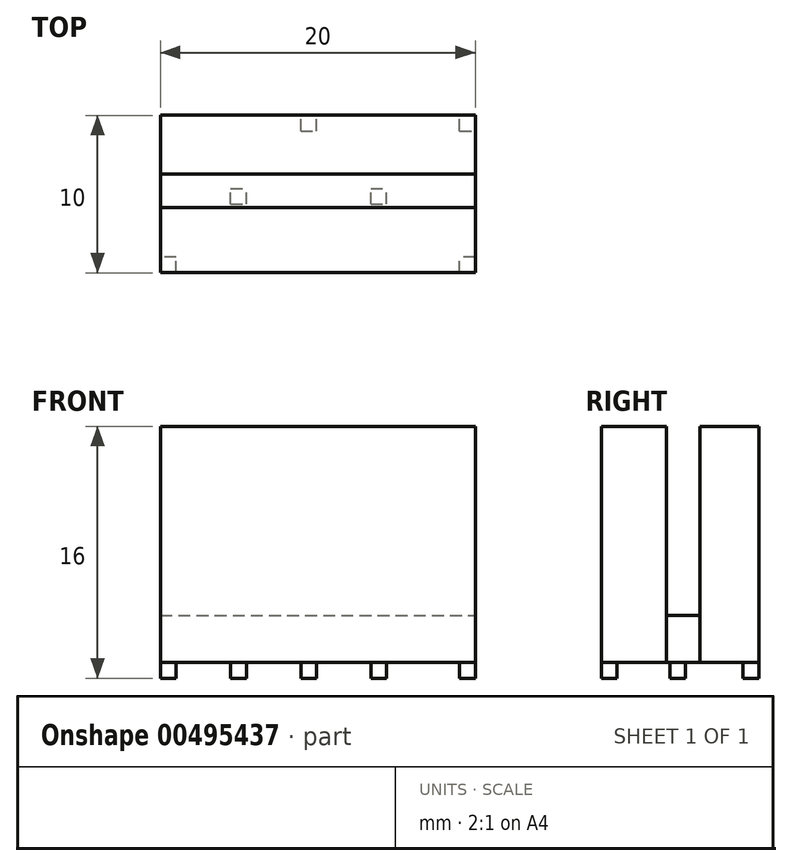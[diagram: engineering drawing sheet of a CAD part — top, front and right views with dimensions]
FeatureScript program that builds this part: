
annotation { "Feature Type Name" : "Feature", "Feature Type Description" : "" }
export const myFeature = defineFeature(function(context is Context, id is Id, definition is map)
    precondition{}
    {
        {
            var Q0;
            Q0=qCreatedBy(makeId("Top.planeOp"),FACE);
            var sketch = newSketch(context, id + "F0", { "sketchPlane" : qUnion([Q0])});
            skLineSegment(sketch, "E0.bottom", {"start": v(-25.14, 12.9) * mm, "end": v(-5.14, 12.9) * mm});
            skLineSegment(sketch, "E0.top", {"start": v(-25.14, 2.9) * mm, "end": v(-5.14, 2.9) * mm});
            skLineSegment(sketch, "E0.left", {"start": v(-25.14, 12.9) * mm, "end": v(-25.14, 2.9) * mm});
            skLineSegment(sketch, "E0.right", {"start": v(-5.14, 12.9) * mm, "end": v(-5.14, 2.9) * mm});
            skLineSegment(sketch, "E1.bottom", {"start": v(-25.14, 9.18) * mm, "end": v(-5.14, 9.18) * mm});
            skLineSegment(sketch, "E1.top", {"start": v(-25.14, 7.05) * mm, "end": v(-5.14, 7.05) * mm});
            skLineSegment(sketch, "E1.left", {"start": v(-25.14, 9.18) * mm, "end": v(-25.14, 7.05) * mm});
            skLineSegment(sketch, "E1.right", {"start": v(-5.14, 9.18) * mm, "end": v(-5.14, 7.05) * mm});
            skSolve(sketch);
        }
        {
            var Q0;
            {var subQ0=sQuery(id+"F0.wireOp",EDGE,"E0.bottom");Q0=makeQuery(id+"F0.imprint","IMPRINT",FACE,{"disambiguationData":[TD([[makeQuery(id+"F0.imprint","IMPRINT",EDGE,{"derivedFrom":subQ0}),-1.0]])]});}
            var Q1;
            {var subQ0=sQuery(id+"F0.wireOp",EDGE,"E0.top");Q1=makeQuery(id+"F0.imprint","IMPRINT",FACE,{"disambiguationData":[TD([[makeQuery(id+"F0.imprint","IMPRINT",EDGE,{"derivedFrom":subQ0}),1.0]])]});}
            extrude(context, id + "F1", {"entities" : qUnion([Q0, Q1]), "depth" : 15 * mm});
        }
        {
            var Q0;
            Q0=makeQuery(id+"F0.imprint","IMPRINT",FACE,{"disambiguationData":[TD([[makeQuery(id+"F0.imprint","IMPRINT",EDGE,{"derivedFrom":sQuery(id+"F0.wireOp",EDGE,"E1.bottom")}),-1.0]])]});
            extrude(context, id + "F2", {"entities" : qUnion([Q0]), "depth" : 3 * mm});
        }
        {
            var Q0;
            {var subQ0=sQuery(id+"F0.wireOp",EDGE,"E0.top");Q0=makeQuery(id+"F0.imprint","IMPRINT",FACE,{"disambiguationData":[TD([[makeQuery(id+"F0.imprint","IMPRINT",EDGE,{"derivedFrom":subQ0}),1.0]])]});}
            var sketch = newSketch(context, id + "F3", { "sketchPlane" : qUnion([Q0])});
            skLineSegment(sketch, "E2.bottom", {"start": v(-25.14, 2.9) * mm, "end": v(-24.14, 2.9) * mm});
            skLineSegment(sketch, "E2.top", {"start": v(-25.14, 12.9) * mm, "end": v(-24.14, 12.9) * mm});
            skLineSegment(sketch, "E2.left", {"start": v(-25.14, 2.9) * mm, "end": v(-25.14, 12.9) * mm});
            skLineSegment(sketch, "E2.right", {"start": v(-24.14, 2.9) * mm, "end": v(-24.14, 3.9) * mm});
            skLineSegment(sketch, "E3.bottom", {"start": v(-25.14, 11.9) * mm, "end": v(-6.14, 11.9) * mm});
            skLineSegment(sketch, "E3.left", {"start": v(-25.14, 11.9) * mm, "end": v(-25.14, 12.9) * mm});
            skLineSegment(sketch, "E3.right", {"start": v(-5.15, 11.9) * mm, "end": v(-5.15, 12.9) * mm});
            skLineSegment(sketch, "E4.bottom", {"start": v(-5.14, 2.9) * mm, "end": v(-6.14, 2.9) * mm});
            skLineSegment(sketch, "E4.top", {"start": v(-5.14, 12.9) * mm, "end": v(-6.14, 12.9) * mm});
            skLineSegment(sketch, "E4.left", {"start": v(-5.14, 2.9) * mm, "end": v(-5.14, 3.9) * mm});
            skLineSegment(sketch, "E4.right", {"start": v(-6.14, 2.9) * mm, "end": v(-6.14, 12.9) * mm});
            skLineSegment(sketch, "E5.bottom", {"start": v(-5.14, 2.9) * mm, "end": v(-25.14, 2.9) * mm});
            skLineSegment(sketch, "E5.top", {"start": v(-5.14, 3.9) * mm, "end": v(-6.14, 3.9) * mm});
            skLineSegment(sketch, "E5.right", {"start": v(-25.14, 2.9) * mm, "end": v(-25.14, 3.9) * mm});
            skLineSegment(sketch, "E6.bottom", {"start": v(-20.69, 2.9) * mm, "end": v(-19.69, 2.9) * mm});
            skLineSegment(sketch, "E6.top", {"start": v(-20.69, 12.9) * mm, "end": v(-19.69, 12.9) * mm});
            skLineSegment(sketch, "E6.left", {"start": v(-20.69, 2.9) * mm, "end": v(-20.69, 12.9) * mm});
            skLineSegment(sketch, "E6.right", {"start": v(-19.69, 2.9) * mm, "end": v(-19.69, 12.9) * mm});
            skLineSegment(sketch, "E7.bottom", {"start": v(-16.22, 2.9) * mm, "end": v(-15.22, 2.9) * mm});
            skLineSegment(sketch, "E7.top", {"start": v(-16.22, 12.9) * mm, "end": v(-15.22, 12.9) * mm});
            skLineSegment(sketch, "E7.left", {"start": v(-16.22, 2.9) * mm, "end": v(-16.22, 12.9) * mm});
            skLineSegment(sketch, "E7.right", {"start": v(-15.22, 2.9) * mm, "end": v(-15.22, 12.9) * mm});
            skLineSegment(sketch, "E8.bottom", {"start": v(-11.77, 2.9) * mm, "end": v(-10.77, 2.9) * mm});
            skLineSegment(sketch, "E8.top", {"start": v(-11.77, 12.9) * mm, "end": v(-10.77, 12.9) * mm});
            skLineSegment(sketch, "E8.left", {"start": v(-11.77, 2.9) * mm, "end": v(-11.77, 12.9) * mm});
            skLineSegment(sketch, "E8.right", {"start": v(-10.77, 2.9) * mm, "end": v(-10.77, 12.9) * mm});
            skLineSegment(sketch, "E9", {"start": v(-24.14, 3.9) * mm, "end": v(-24.14, 11.9) * mm});
            skLineSegment(sketch, "E10", {"start": v(-24.14, 11.9) * mm, "end": v(-24.14, 12.9) * mm});
            skLineSegment(sketch, "E11", {"start": v(-6.14, 11.9) * mm, "end": v(-5.15, 11.9) * mm});
            skLineSegment(sketch, "E12", {"start": v(-6.14, 3.9) * mm, "end": v(-25.14, 3.9) * mm});
            skLineSegment(sketch, "E13.bottom", {"start": v(-25.14, 7.26) * mm, "end": v(-5.14, 7.26) * mm});
            skLineSegment(sketch, "E13.top", {"start": v(-25.14, 8.26) * mm, "end": v(-5.14, 8.26) * mm});
            skLineSegment(sketch, "E13.left", {"start": v(-25.14, 7.26) * mm, "end": v(-25.14, 8.26) * mm});
            skLineSegment(sketch, "E13.right", {"start": v(-5.14, 7.26) * mm, "end": v(-5.14, 8.26) * mm});
            skLineSegment(sketch, "E14", {"start": v(-24.14, 12.9) * mm, "end": v(-5.15, 12.9) * mm});
            skLineSegment(sketch, "E15", {"start": v(-5.14, 3.9) * mm, "end": v(-5.14, 12.9) * mm});
            skSolve(sketch);
        }
        {
            var Q0;
            {var subQ0=sQuery(id+"F3.wireOp",EDGE,"E2.right");Q0=makeQuery(id+"F3.imprint","IMPRINT",FACE,{"disambiguationData":[TD([[makeQuery(id+"F3.imprint","IMPRINT",EDGE,{"derivedFrom":subQ0}),1.0]])]});}
            var Q1;
            {var subQ5=sQuery(id+"F3.wireOp",EDGE,"E5.top");Q1=makeQuery(id+"F3.imprint","IMPRINT",FACE,{"disambiguationData":[TD([[makeQuery(id+"F3.imprint","IMPRINT",EDGE,{"derivedFrom":subQ5}),1.0]])]});}
            var Q2;
            {var subQ0=sQuery(id+"F3.wireOp",EDGE,"E3.right");Q2=makeQuery(id+"F3.imprint","IMPRINT",FACE,{"disambiguationData":[TD([[makeQuery(id+"F3.imprint","IMPRINT",EDGE,{"derivedFrom":subQ0}),1.0]])]});}
            var Q3;
            {var subQ0=sQuery(id+"F3.wireOp",EDGE,"E13.bottom");var subQ1=sQuery(id+"F3.wireOp",EDGE,"E8.left");var subQ2=makeQuery(id+"F3.imprint","INTERSECT",VERTEX,{"derivedFrom":[subQ1,subQ0]});Q3=makeQuery(id+"F3.imprint","IMPRINT",FACE,{"disambiguationData":[TD([[makeQuery(id+"F3.imprint","IMPRINT",EDGE,{"disambiguationData":[TD([[subQ2,-1.0]])],"derivedFrom":subQ1}),-1.0]])]});}
            var Q4;
            {var subQ0=sQuery(id+"F3.wireOp",EDGE,"E13.bottom");var subQ1=sQuery(id+"F3.wireOp",EDGE,"E6.left");var subQ2=makeQuery(id+"F3.imprint","INTERSECT",VERTEX,{"derivedFrom":[subQ1,subQ0]});Q4=makeQuery(id+"F3.imprint","IMPRINT",FACE,{"disambiguationData":[TD([[makeQuery(id+"F3.imprint","IMPRINT",EDGE,{"disambiguationData":[TD([[subQ2,-1.0]])],"derivedFrom":subQ1}),-1.0]])]});}
            var Q5;
            Q5=makeQuery(id+"F3.imprint","IMPRINT",FACE,{"disambiguationData":[TD([[makeQuery(id+"F3.imprint","IMPRINT",EDGE,{"derivedFrom":sQuery(id+"F3.wireOp",EDGE,"E2.top")}),-1.0]])]});
            var Q6;
            {var subQ0=sQuery(id+"F3.wireOp",EDGE,"E7.left");var subQ1=sQuery(id+"F3.wireOp",EDGE,"E3.bottom");var subQ2=makeQuery(id+"F3.imprint","INTERSECT",VERTEX,{"derivedFrom":[subQ1,subQ0]});Q6=makeQuery(id+"F3.imprint","IMPRINT",FACE,{"disambiguationData":[TD([[makeQuery(id+"F3.imprint","IMPRINT",EDGE,{"disambiguationData":[TD([[subQ2,-1.0]])],"derivedFrom":subQ1}),1.0]])]});}
            var Q7;
            {var subQ0=sQuery(id+"F3.wireOp",EDGE,"E7.bottom");Q7=makeQuery(id+"F3.imprint","IMPRINT",FACE,{"disambiguationData":[TD([[makeQuery(id+"F3.imprint","IMPRINT",EDGE,{"derivedFrom":subQ0}),1.0]])]});}
            extrude(context, id + "F4", {"entities" : qUnion([Q0, Q1, Q2, Q3, Q4, Q5, Q6, Q7]), "depth" : -1 * mm});
        }
    });
